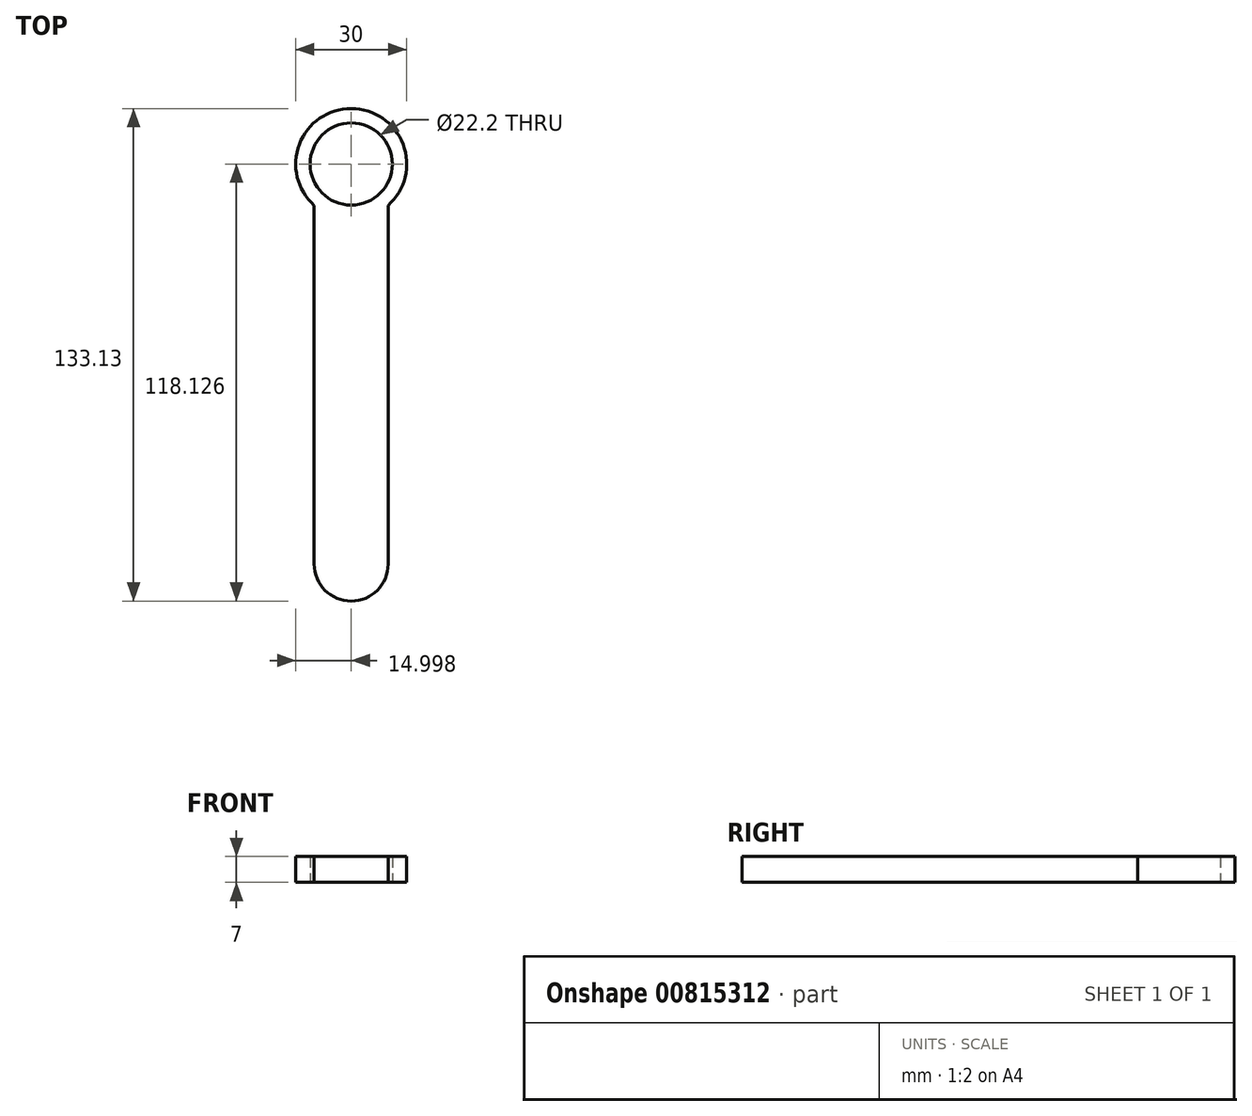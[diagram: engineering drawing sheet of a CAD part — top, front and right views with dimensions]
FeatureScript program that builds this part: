
annotation { "Feature Type Name" : "Feature", "Feature Type Description" : "" }
export const myFeature = defineFeature(function(context is Context, id is Id, definition is map)
    precondition{}
    {
        {
            var Q0;
            Q0=qCreatedBy(makeId("Top.planeOp"),FACE);
            var sketch = newSketch(context, id + "F0", { "sketchPlane" : qUnion([Q0])});
            skLineSegment(sketch, "E0.bottom", {"start": v(-7.71, -74.17) * mm, "end": v(12.29, -74.17) * mm});
            skLineSegment(sketch, "E0.top", {"start": v(-7.71, 45.83) * mm, "end": v(12.29, 45.83) * mm});
            skLineSegment(sketch, "E0.left", {"start": v(-7.71, -74.17) * mm, "end": v(-7.71, 45.83) * mm});
            skLineSegment(sketch, "E0.right", {"start": v(12.29, -74.17) * mm, "end": v(12.29, 45.83) * mm});
            skCircle(sketch, "E1", {"center": v(2.29, 45.83) * mm, "radius": 15 * mm});
            skCircle(sketch, "E2", {"center": v(2.29, 45.83) * mm, "radius": 11.1 * mm});
            skLineSegment(sketch, "E3", {"start": v(-7.71, -74.17) * mm, "end": v(2.29, -74.17) * mm});
            skLineSegment(sketch, "E4", {"start": v(-7.71, -74.17) * mm, "end": v(-7.71, -62.3) * mm});
            skCircle(sketch, "E5", {"center": v(2.29, -62.3) * mm, "radius": 10 * mm});
            skSolve(sketch);
        }
        {
            var Q0;
            {var subQ0=sQuery(id+"F0.wireOp",EDGE,"E5");var subQ5=sQuery(id+"F0.wireOp",EDGE,"E0.right");var subQ7=makeQuery(id+"F0.imprint","INTERSECT",VERTEX,{"derivedFrom":[subQ5,subQ0]});Q0=makeQuery(id+"F0.imprint","IMPRINT",FACE,{"disambiguationData":[TD([[makeQuery(id+"F0.imprint","IMPRINT",EDGE,{"disambiguationData":[TD([[subQ7,-1.0]])],"derivedFrom":subQ5}),1.0]])]});}
            var Q1;
            {var subQ0=sQuery(id+"F0.wireOp",EDGE,"E5");var subQ2=makeQuery(id+"F0.imprint","INTERSECT",VERTEX,{"derivedFrom":[sQuery(id+"F0.wireOp",EDGE,"E0.right"),subQ0]});Q1=makeQuery(id+"F0.imprint","IMPRINT",FACE,{"disambiguationData":[TD([[makeQuery(id+"F0.imprint","IMPRINT",EDGE,{"disambiguationData":[TD([[subQ2,-1.0]])],"derivedFrom":subQ0}),1.0]])]});}
            var Q2;
            {var subQ0=sQuery(id+"F0.wireOp",EDGE,"E1");var subQ1=sQuery(id+"F0.wireOp",EDGE,"E0.left");var subQ2=makeQuery(id+"F0.imprint","INTERSECT",VERTEX,{"derivedFrom":[subQ1,subQ0]});Q2=makeQuery(id+"F0.imprint","IMPRINT",FACE,{"disambiguationData":[TD([[makeQuery(id+"F0.imprint","IMPRINT",EDGE,{"disambiguationData":[TD([[subQ2,-1.0]])],"derivedFrom":subQ1}),1.0]])]});}
            var Q3;
            {var subQ0=sQuery(id+"F0.wireOp",EDGE,"E1");var subQ1=sQuery(id+"F0.wireOp",EDGE,"E0.left");var subQ2=makeQuery(id+"F0.imprint","INTERSECT",VERTEX,{"derivedFrom":[subQ1,subQ0]});Q3=makeQuery(id+"F0.imprint","IMPRINT",FACE,{"disambiguationData":[TD([[makeQuery(id+"F0.imprint","IMPRINT",EDGE,{"disambiguationData":[TD([[subQ2,-1.0]])],"derivedFrom":subQ1}),-1.0]])]});}
            extrude(context, id + "F1", {"entities" : qUnion([Q0, Q1, Q2, Q3]), "depth" : 7 * mm, "offsetDistance" : 25 * mm});
        }
    });
